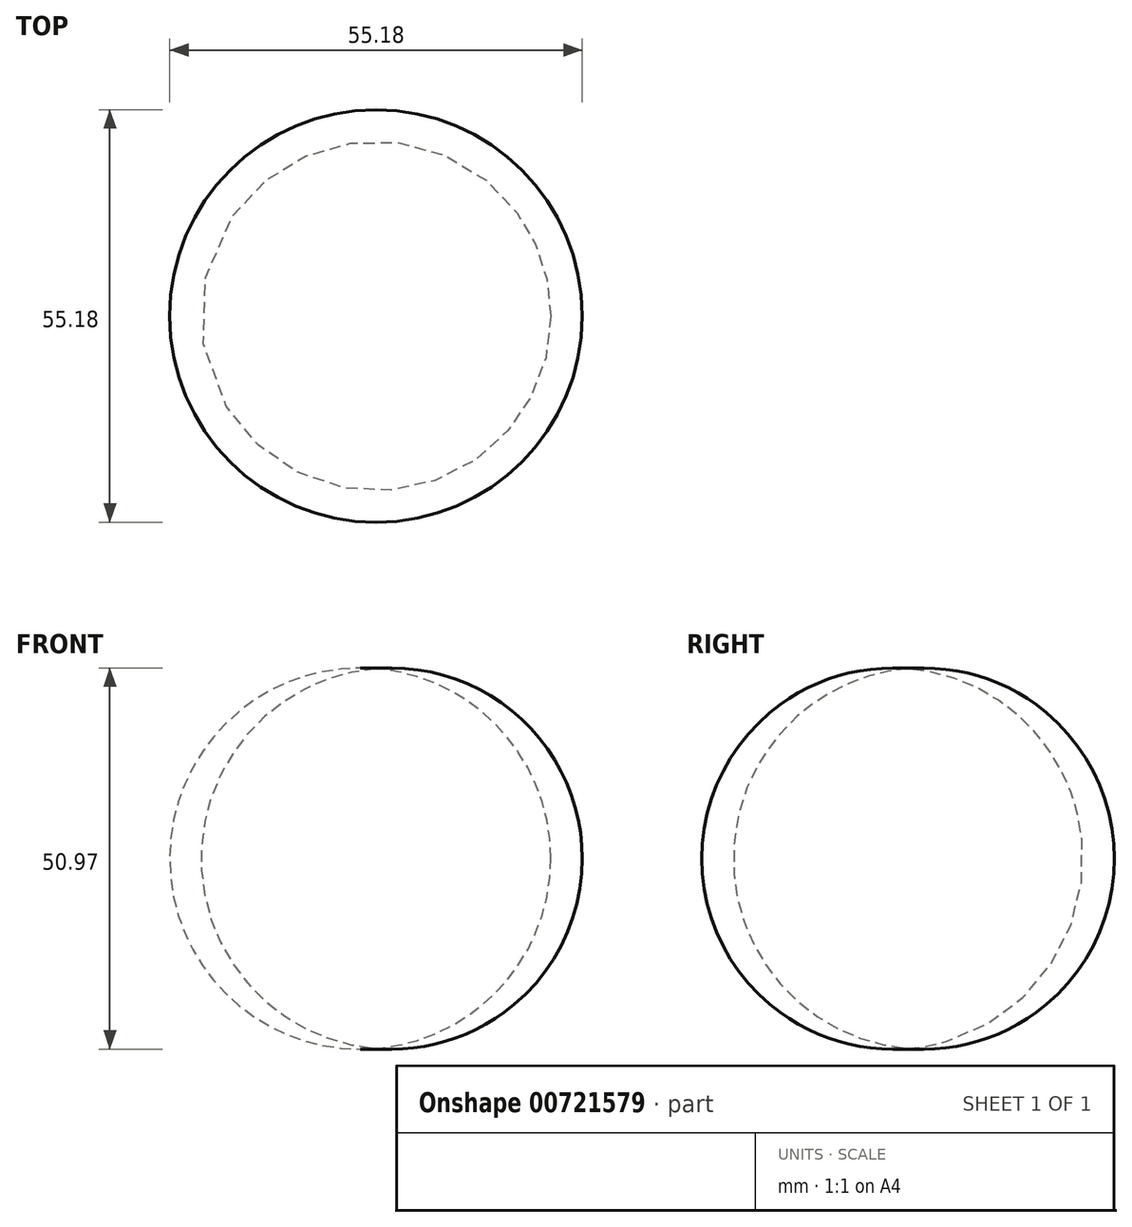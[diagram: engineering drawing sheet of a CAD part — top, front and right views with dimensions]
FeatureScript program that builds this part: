
annotation { "Feature Type Name" : "Feature", "Feature Type Description" : "" }
export const myFeature = defineFeature(function(context is Context, id is Id, definition is map)
    precondition{}
    {
        {
            var Q0;
            Q0=qCreatedBy(makeId("Front.planeOp"),FACE);
            var sketch = newSketch(context, id + "F0", { "sketchPlane" : qUnion([Q0])});
            skLineSegment(sketch, "E0", {"start": v(0, -22.3) * mm, "end": v(0, 28.5) * mm});
            skArc(sketch, "E1", {"start": v(0, -22.3) * mm, "mid": v(23.38, 3.1) * mm, "end": v(0, 28.5) * mm});
            skSolve(sketch);
        }
        {
            var Q0;
            Q0 = qSketchRegion(id + "F0", true);
            var Q1;
            Q1=sQuery(id+"F0.wireOp",EDGE,"E0");
            revolve(context, id + "F1", {"surfaceOperationType" : NewSurfaceOperationType.NEW, "entities" : qUnion([Q0]), "axis" : qUnion([Q1]), "revolveType" : RevolveType.FULL});
        }
    });
